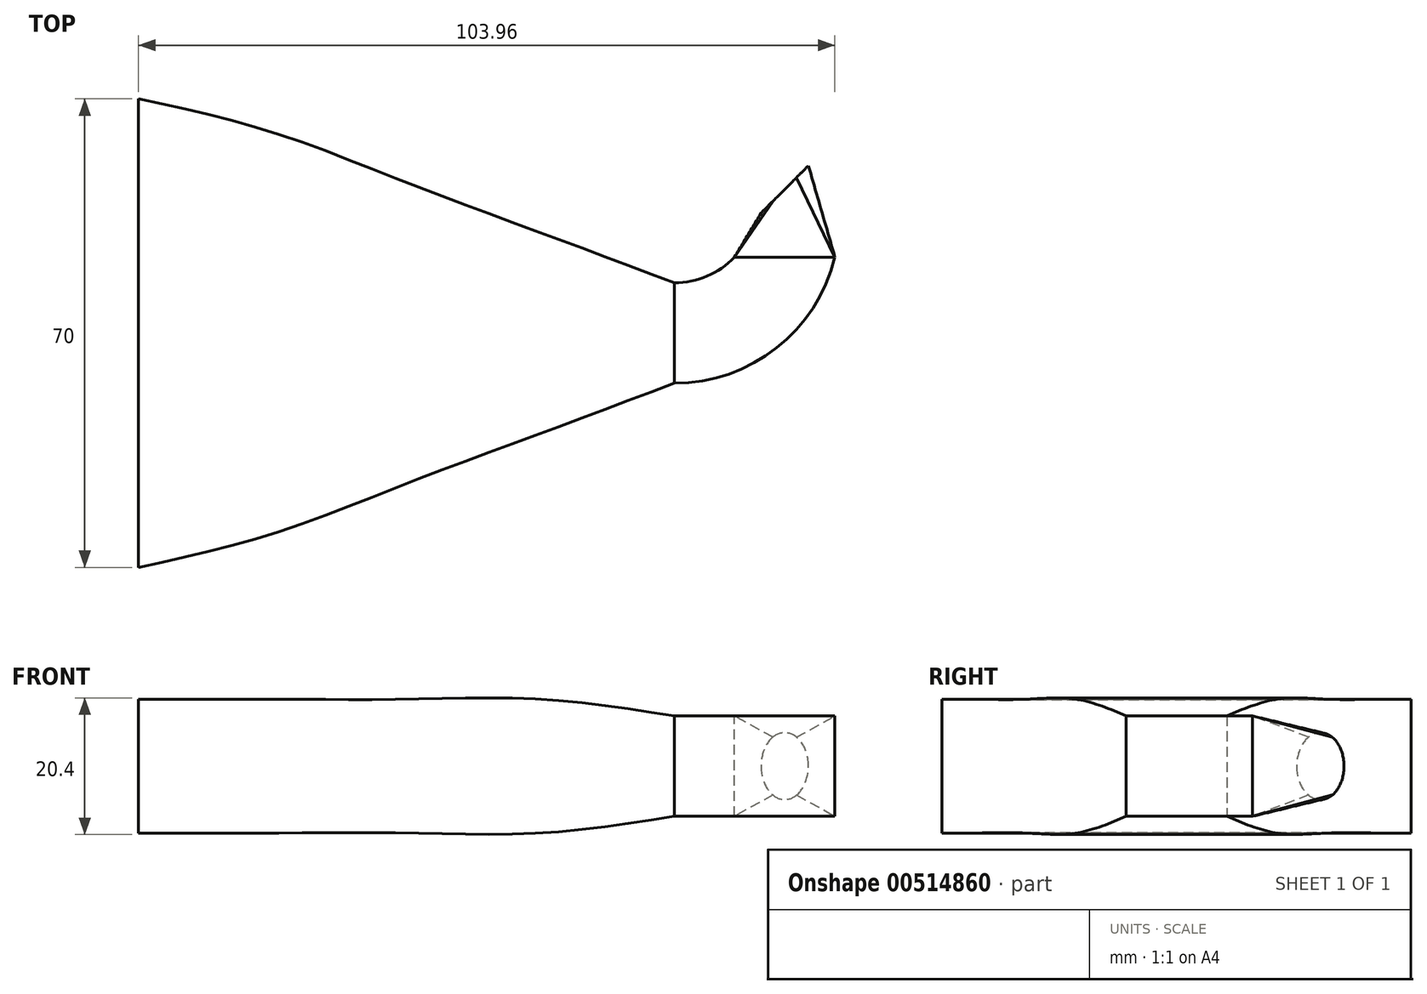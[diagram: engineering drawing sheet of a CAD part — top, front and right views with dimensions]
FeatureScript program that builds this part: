
annotation { "Feature Type Name" : "Feature", "Feature Type Description" : "" }
export const myFeature = defineFeature(function(context is Context, id is Id, definition is map)
    precondition{}
    {
        {
            var Q0;
            Q0=qCreatedBy(makeId("Top.planeOp"),FACE);
            var sketch = newSketch(context, id + "F0", { "sketchPlane" : qUnion([Q0])});
            skLineSegment(sketch, "E0.left", {"start": v(-50, 50) * mm, "end": v(-50, -50) * mm});
            skPoint(sketch, "E0.middle", {"position": v(0, 0) * mm});
            skLineSegment(sketch, "E1", {"start": v(-50, 50) * mm, "end": v(-50, 40) * mm});
            skLineSegment(sketch, "E2", {"start": v(50, 40) * mm, "end": v(42.93, 32.93) * mm});
            skLineSegment(sketch, "E3", {"start": v(42.93, 32.93) * mm, "end": v(46.46, 36.46) * mm});
            skLineSegment(sketch, "E4", {"start": v(-50, 0) * mm, "end": v(-50, -10) * mm});
            skLineSegment(sketch, "E5", {"start": v(-50, -10) * mm, "end": v(-50, 15) * mm});
            skLineSegment(sketch, "E6", {"start": v(-50, 15) * mm, "end": v(114.78, 15) * mm});
            skLineSegment(sketch, "E7", {"start": v(42.93, 32.93) * mm, "end": v(42.93, -37.04) * mm});
            skLineSegment(sketch, "E8", {"start": v(-50, 15) * mm, "end": v(30, 15) * mm});
            skLineSegment(sketch, "E9", {"start": v(30, 15) * mm, "end": v(30, 30) * mm});
            skLineSegment(sketch, "E10", {"start": v(30, 15) * mm, "end": v(30, 0) * mm});
            skLineSegment(sketch, "E11", {"start": v(42.93, 32.93) * mm, "end": v(81, 32.93) * mm});
            skLineSegment(sketch, "E12", {"start": v(46.46, 36.46) * mm, "end": v(46.46, 32.93) * mm});
            skLineSegment(sketch, "E13", {"start": v(46.46, 36.46) * mm, "end": v(46.46, 0) * mm});
            skLineSegment(sketch, "E14", {"start": v(46.46, 36.46) * mm, "end": v(62.14, 20.79) * mm});
            skLineSegment(sketch, "E15", {"start": v(-50, 50) * mm, "end": v(-109.66, 50) * mm});
            skLineSegment(sketch, "E16", {"start": v(-50, 40) * mm, "end": v(-110.5, 40) * mm});
            skLineSegment(sketch, "E17", {"start": v(-50, 15) * mm, "end": v(-113.83, 15) * mm});
            skLineSegment(sketch, "E18", {"start": v(-50, 0) * mm, "end": v(-113, 0) * mm});
            skLineSegment(sketch, "E19", {"start": v(-50, -10) * mm, "end": v(-113, -10) * mm});
            skLineSegment(sketch, "E20", {"start": v(-50, -50) * mm, "end": v(-111.33, -50) * mm});
            skLineSegment(sketch, "E21", {"start": v(30, 30) * mm, "end": v(95.7, 30) * mm});
            skPoint(sketch, "E22", {"position": v(42.93, 30) * mm});
            skPoint(sketch, "E23", {"position": v(46.46, 30) * mm});
            skPoint(sketch, "E24", {"position": v(42.93, 26.34) * mm});
            skLineSegment(sketch, "E25", {"start": v(30, 15) * mm, "end": v(30, 7.5) * mm});
            skLineSegment(sketch, "E26", {"start": v(30, 15) * mm, "end": v(30, 22.5) * mm});
            skLineSegment(sketch, "E27", {"start": v(30, 15) * mm, "end": v(0, 15) * mm});
            skLineSegment(sketch, "E28", {"start": v(-50, 15) * mm, "end": v(-30, 15) * mm});
            skLineSegment(sketch, "E29", {"start": v(-30, 15) * mm, "end": v(-10, 15) * mm});
            skLineSegment(sketch, "E30", {"start": v(-10, 15) * mm, "end": v(10, 15) * mm});
            skSolve(sketch);
        }
        {
            var Q0;
            Q0=sQuery(id+"F0.wireOp",EDGE,"E2");
            cPlane(context, id + "F1", {"entities" : qUnion([Q0]), "cplaneType" : CPlaneType.LINE_ANGLE, "offset" : 25 * mm, "angle" : 90 * degree, "width" : 150 * mm, "height" : 150 * mm});
        }
        {
            var Q0;
            Q0=qCreatedBy(id+"F1.planeOp",FACE);
            var sketch = newSketch(context, id + "F2", { "sketchPlane" : qUnion([Q0])});
            skCircle(sketch, "E31", {"center": v(58.64, 0) * mm, "radius": 5 * mm});
            skSolve(sketch);
        }
        {
            var Q0;
            Q0=sQuery(id+"F0.wireOp",VERTEX,"E6.start");
            var Q1;
            Q1=qCreatedBy(makeId("Right.planeOp"),FACE);
            cPlane(context, id + "F3", {"entities" : qUnion([Q0, Q1]), "cplaneType" : CPlaneType.PLANE_POINT, "offset" : 25 * mm, "width" : 150 * mm, "height" : 150 * mm});
        }
        {
            var Q0;
            Q0=qCreatedBy(id+"F3.planeOp",FACE);
            var sketch = newSketch(context, id + "F4", { "sketchPlane" : qUnion([Q0])});
            skPoint(sketch, "E32", {"position": v(15, 0) * mm});
            skLineSegment(sketch, "E33", {"start": v(50, 10) * mm, "end": v(-20, 10) * mm});
            skLineSegment(sketch, "E34", {"start": v(50, -10) * mm, "end": v(-20, -10) * mm});
            skLineSegment(sketch, "E35", {"start": v(50, 10) * mm, "end": v(50, -10) * mm});
            skLineSegment(sketch, "E36", {"start": v(-20, 10) * mm, "end": v(-20, -10) * mm});
            skSolve(sketch);
        }
        {
            var Q0;
            Q0=sQuery(id+"F0.wireOp",VERTEX,"E9.start");
            var Q1;
            Q1=qCreatedBy(id+"F3.planeOp",FACE);
            var Q2;
            Q2=qBodyType(qCreatedBy(id+"FoWz66eWp3AvkS4_1",EDGE),BodyType.WIRE);
            cPlane(context, id + "F5", {"entities" : qUnion([Q0, Q1, Q2]), "cplaneType" : CPlaneType.PLANE_POINT, "offset" : 25 * mm, "width" : 150 * mm, "height" : 150 * mm});
        }
        {
            var Q0;
            Q0=qCreatedBy(id+"F5.planeOp",FACE);
            var sketch = newSketch(context, id + "F6", { "sketchPlane" : qUnion([Q0])});
            skLineSegment(sketch, "E37", {"start": v(22.5, 7.5) * mm, "end": v(7.5, 7.5) * mm});
            skLineSegment(sketch, "E38", {"start": v(22.5, -7.5) * mm, "end": v(7.5, -7.5) * mm});
            skLineSegment(sketch, "E39", {"start": v(22.5, 7.5) * mm, "end": v(22.5, -7.5) * mm});
            skLineSegment(sketch, "E40", {"start": v(7.5, 7.5) * mm, "end": v(7.5, -7.5) * mm});
            skSolve(sketch);
        }
        {
            var Q0;
            Q0=qCreatedBy(makeId("Front.planeOp"),FACE);
            var Q1;
            Q1=sQuery(id+"F0.wireOp",VERTEX,"E24");
            cPlane(context, id + "F7", {"entities" : qUnion([Q0, Q1]), "cplaneType" : CPlaneType.PLANE_POINT, "offset" : 25 * mm, "width" : 150 * mm, "height" : 150 * mm});
        }
        {
            var Q0;
            Q0=qCreatedBy(id+"F7.planeOp",FACE);
            var sketch = newSketch(context, id + "F8", { "sketchPlane" : qUnion([Q0])});
            skPoint(sketch, "E41", {"position": v(46.46, 0) * mm});
            skLineSegment(sketch, "E42", {"start": v(38.96, 0) * mm, "end": v(38.96, -7.5) * mm});
            skLineSegment(sketch, "E43", {"start": v(38.96, 0) * mm, "end": v(38.96, 7.5) * mm});
            skLineSegment(sketch, "E44", {"start": v(53.96, 0) * mm, "end": v(53.96, -7.5) * mm});
            skLineSegment(sketch, "E45", {"start": v(53.96, 0) * mm, "end": v(53.96, 7.5) * mm});
            skLineSegment(sketch, "E46", {"start": v(38.96, -7.5) * mm, "end": v(53.96, -7.5) * mm});
            skLineSegment(sketch, "E47", {"start": v(38.96, 7.5) * mm, "end": v(53.96, 7.5) * mm});
            skSolve(sketch);
        }
        {
            var Q0;
            Q0=makeQuery(id+"F2.imprint","IMPRINT",FACE,{"disambiguationData":[TD([[makeQuery(id+"F2.imprint","IMPRINT",EDGE,{"derivedFrom":sQuery(id+"F2.wireOp",EDGE,"E31")}),1.0]])]});
            var Q1;
            Q1=makeQuery(id+"F8.imprint","IMPRINT",FACE,{"disambiguationData":[TD([[makeQuery(id+"F8.imprint","IMPRINT",EDGE,{"derivedFrom":sQuery(id+"F8.wireOp",EDGE,"E42")}),1.0]])]});
            loft(context, id + "F9", {"sheetProfilesArray" : [{ "sheetProfileEntities" : qUnion([Q0]) }, { "sheetProfileEntities" : qUnion([Q1]) }]});
        }
        {
            var Q0;
            Q0=sQuery(id+"F0.wireOp",VERTEX,"E17.start");
            var Q1;
            Q1=qCreatedBy(makeId("Right.planeOp"),FACE);
            cPlane(context, id + "F10", {"entities" : qUnion([Q0, Q1]), "cplaneType" : CPlaneType.PLANE_POINT, "offset" : 25 * mm, "width" : 150 * mm, "height" : 150 * mm});
        }
        {
            var Q0;
            Q0=sQuery(id+"F0.wireOp",VERTEX,"E30.end");
            var Q1;
            Q1=qCreatedBy(id+"F5.planeOp",FACE);
            cPlane(context, id + "F11", {"entities" : qUnion([Q0, Q1]), "cplaneType" : CPlaneType.PLANE_POINT, "offset" : 25 * mm, "width" : 150 * mm, "height" : 150 * mm});
        }
        {
            var Q0;
            Q0=qCreatedBy(id+"F11.planeOp",FACE);
            var sketch = newSketch(context, id + "F12", { "sketchPlane" : qUnion([Q0])});
            skPoint(sketch, "E48", {"position": v(15, 0) * mm});
            skLineSegment(sketch, "E49", {"start": v(30, -10) * mm, "end": v(30, 10) * mm});
            skLineSegment(sketch, "E50", {"start": v(0, 10) * mm, "end": v(0, -10) * mm});
            skLineSegment(sketch, "E51", {"start": v(30, 10) * mm, "end": v(0, 10) * mm});
            skLineSegment(sketch, "E52", {"start": v(30, -10) * mm, "end": v(0, -10) * mm});
            skSolve(sketch);
        }
        {
            var Q0;
            Q0=sQuery(id+"F0.wireOp",VERTEX,"E30.start");
            var Q1;
            Q1=qCreatedBy(makeId("Right.planeOp"),FACE);
            cPlane(context, id + "F13", {"entities" : qUnion([Q0, Q1]), "cplaneType" : CPlaneType.PLANE_POINT, "offset" : 25 * mm, "width" : 150 * mm, "height" : 150 * mm});
        }
        {
            var Q0;
            Q0=qCreatedBy(id+"F13.planeOp",FACE);
            var sketch = newSketch(context, id + "F14", { "sketchPlane" : qUnion([Q0])});
            skPoint(sketch, "E53", {"position": v(15, 0) * mm});
            skLineSegment(sketch, "E54", {"start": v(-7.5, -10) * mm, "end": v(-7.5, 10) * mm});
            skLineSegment(sketch, "E55", {"start": v(37.5, -10) * mm, "end": v(37.5, 10) * mm});
            skLineSegment(sketch, "E56", {"start": v(37.5, 10) * mm, "end": v(-7.5, 10) * mm});
            skLineSegment(sketch, "E57", {"start": v(37.5, -10) * mm, "end": v(-7.5, -10) * mm});
            skSolve(sketch);
        }
        {
            var Q0;
            Q0=sQuery(id+"F0.wireOp",VERTEX,"E29.start");
            var Q1;
            Q1=qCreatedBy(id+"F13.planeOp",FACE);
            cPlane(context, id + "F15", {"entities" : qUnion([Q0, Q1]), "cplaneType" : CPlaneType.PLANE_POINT, "offset" : 25 * mm, "width" : 150 * mm, "height" : 150 * mm});
        }
        {
            var Q0;
            Q0=qCreatedBy(id+"F15.planeOp",FACE);
            var sketch = newSketch(context, id + "F16", { "sketchPlane" : qUnion([Q0])});
            skPoint(sketch, "E58", {"position": v(15, 0) * mm});
            skLineSegment(sketch, "E59", {"start": v(45, 10) * mm, "end": v(45, -10) * mm});
            skLineSegment(sketch, "E60", {"start": v(-15, 10) * mm, "end": v(-15, -10) * mm});
            skLineSegment(sketch, "E61", {"start": v(45, -10) * mm, "end": v(-15, -10) * mm});
            skLineSegment(sketch, "E62", {"start": v(45, 10) * mm, "end": v(-15, 10) * mm});
            skSolve(sketch);
        }
        {
            var Q0;
            Q0=sQuery(id+"F8.wireOp",VERTEX,"E42.start");
            var Q1;
            Q1=qCreatedBy(makeId("Top.planeOp"),FACE);
            cPlane(context, id + "F17", {"entities" : qUnion([Q0, Q1]), "cplaneType" : CPlaneType.PLANE_POINT, "offset" : 25 * mm, "width" : 150 * mm, "height" : 150 * mm});
        }
        {
            var Q0;
            Q0=qCreatedBy(id+"F17.planeOp",FACE);
            var sketch = newSketch(context, id + "F18", { "sketchPlane" : qUnion([Q0])});
            skPoint(sketch, "E63", {"position": v(30, 22.5) * mm});
            skPoint(sketch, "E64", {"position": v(38.96, 26.34) * mm});
            skPoint(sketch, "E65", {"position": v(30, 7.5) * mm});
            skPoint(sketch, "E66", {"position": v(53.96, 26.34) * mm});
            skArc(sketch, "E67", {"start": v(30, 22.5) * mm, "mid": v(34.88, 23.5) * mm, "end": v(38.96, 26.34) * mm});
            skArc(sketch, "E68", {"start": v(30, 7.5) * mm, "mid": v(45.24, 12.77) * mm, "end": v(53.96, 26.34) * mm});
            skLineSegment(sketch, "E69", {"start": v(30, 22.5) * mm, "end": v(30, 7.5) * mm});
            skLineSegment(sketch, "E70", {"start": v(38.96, 26.34) * mm, "end": v(53.96, 26.34) * mm});
            skSolve(sketch);
        }
        {
            var Q0;
            Q0=makeQuery(id+"F4.imprint","IMPRINT",FACE,{"disambiguationData":[TD([[makeQuery(id+"F4.imprint","IMPRINT",EDGE,{"derivedFrom":sQuery(id+"F4.wireOp",EDGE,"E33")}),1.0]])]});
            var Q1;
            Q1=makeQuery(id+"F16.imprint","IMPRINT",FACE,{"disambiguationData":[TD([[makeQuery(id+"F16.imprint","IMPRINT",EDGE,{"derivedFrom":sQuery(id+"F16.wireOp",EDGE,"E59")}),-1.0]])]});
            var Q2;
            Q2=makeQuery(id+"F14.imprint","IMPRINT",FACE,{"disambiguationData":[TD([[makeQuery(id+"F14.imprint","IMPRINT",EDGE,{"derivedFrom":sQuery(id+"F14.wireOp",EDGE,"E54")}),-1.0]])]});
            var Q3;
            Q3=makeQuery(id+"F12.imprint","IMPRINT",FACE,{"disambiguationData":[TD([[makeQuery(id+"F12.imprint","IMPRINT",EDGE,{"derivedFrom":sQuery(id+"F12.wireOp",EDGE,"E49")}),1.0]])]});
            var Q4;
            Q4=makeQuery(id+"F6.imprint","IMPRINT",FACE,{"disambiguationData":[TD([[makeQuery(id+"F6.imprint","IMPRINT",EDGE,{"derivedFrom":sQuery(id+"F6.wireOp",EDGE,"E37")}),1.0]])]});
            loft(context, id + "F19", {"sheetProfilesArray" : [{ "sheetProfileEntities" : qUnion([Q0]) }, { "sheetProfileEntities" : qUnion([Q1]) }, { "sheetProfileEntities" : qUnion([Q2]) }, { "sheetProfileEntities" : qUnion([Q3]) }, { "sheetProfileEntities" : qUnion([Q4]) }]});
        }
        {
            var Q0;
            Q0=makeQuery(id+"F18.imprint","IMPRINT",FACE,{"disambiguationData":[TD([[makeQuery(id+"F18.imprint","IMPRINT",EDGE,{"derivedFrom":sQuery(id+"F18.wireOp",EDGE,"E67")}),-1.0]])]});
            extrude(context, id + "F20", {"entities" : qUnion([Q0]), "operationType" : NewBodyOperationType.ADD, "endBound" : BoundingType.SYMMETRIC, "depth" : 15 * mm, "offsetDistance" : 25 * mm});
        }
    });
